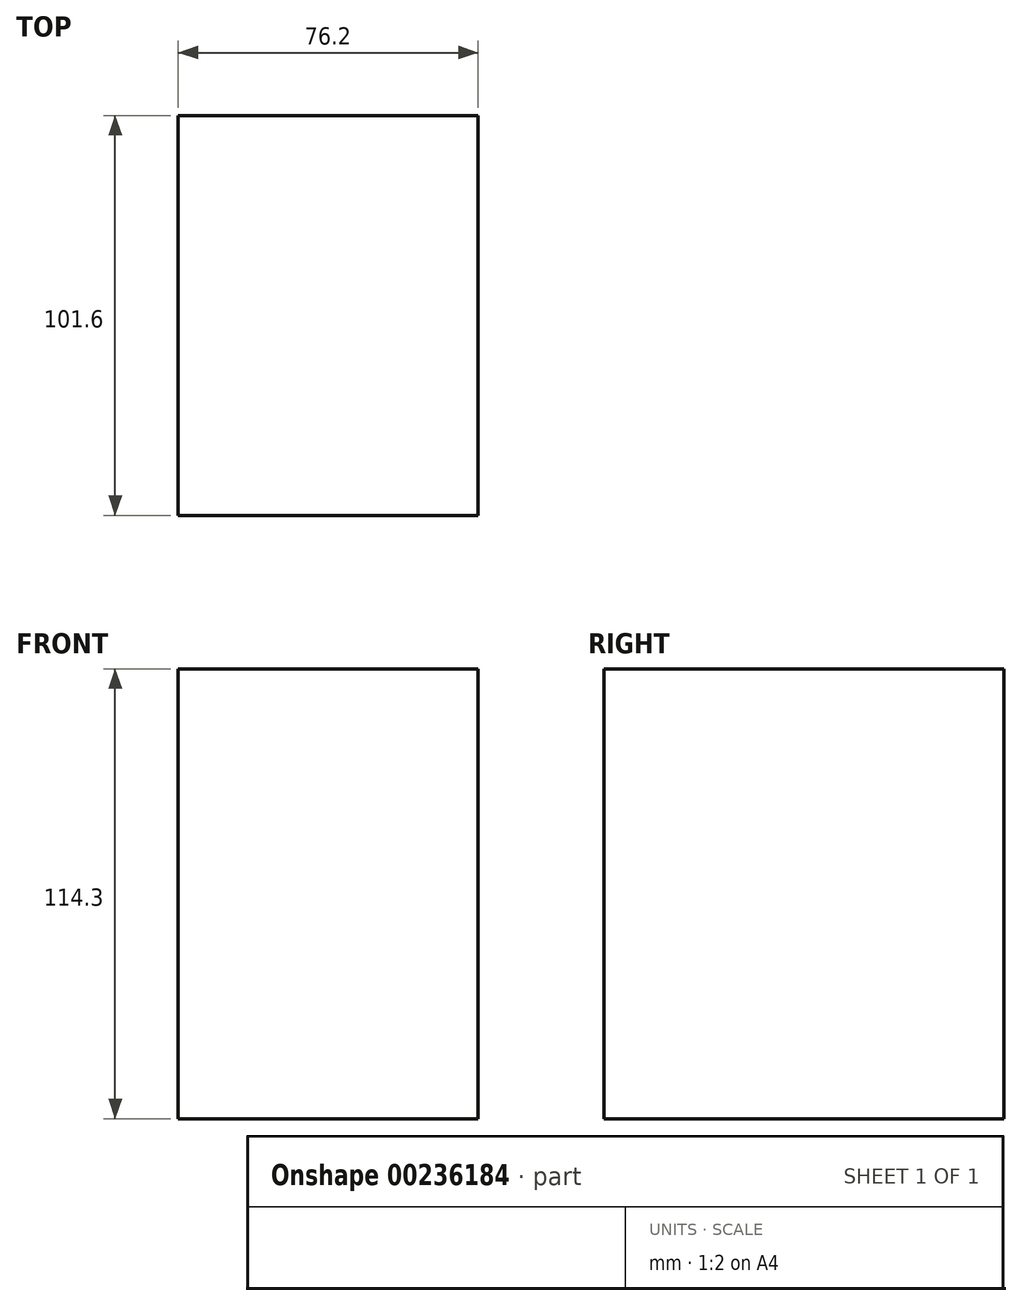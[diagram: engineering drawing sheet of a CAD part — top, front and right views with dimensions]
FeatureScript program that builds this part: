
annotation { "Feature Type Name" : "Feature", "Feature Type Description" : "" }
export const myFeature = defineFeature(function(context is Context, id is Id, definition is map)
    precondition{}
    {
        {
            var Q0;
            Q0=qCreatedBy(makeId("Front.planeOp"),FACE);
            var sketch = newSketch(context, id + "F0", { "sketchPlane" : qUnion([Q0])});
            skLineSegment(sketch, "E0.bottom", {"start": v(0, 0) * mm, "end": v(76.2, 0) * mm});
            skLineSegment(sketch, "E0.top", {"start": v(0, 114.3) * mm, "end": v(76.2, 114.3) * mm});
            skLineSegment(sketch, "E0.left", {"start": v(0, 0) * mm, "end": v(0, 114.3) * mm});
            skLineSegment(sketch, "E0.right", {"start": v(76.2, 0) * mm, "end": v(76.2, 114.3) * mm});
            skSolve(sketch);
        }
        {
            var Q0;
            Q0=makeQuery(id+"F0.imprint","IMPRINT",FACE,{"disambiguationData":[TD([[makeQuery(id+"F0.imprint","IMPRINT",EDGE,{"derivedFrom":sQuery(id+"F0.wireOp",EDGE,"E0.bottom")}),1.0]])]});
            extrude(context, id + "F1", {"entities" : qUnion([Q0]), "oppositeDirection" : true, "depth" : 101.6 * mm});
        }
    });
